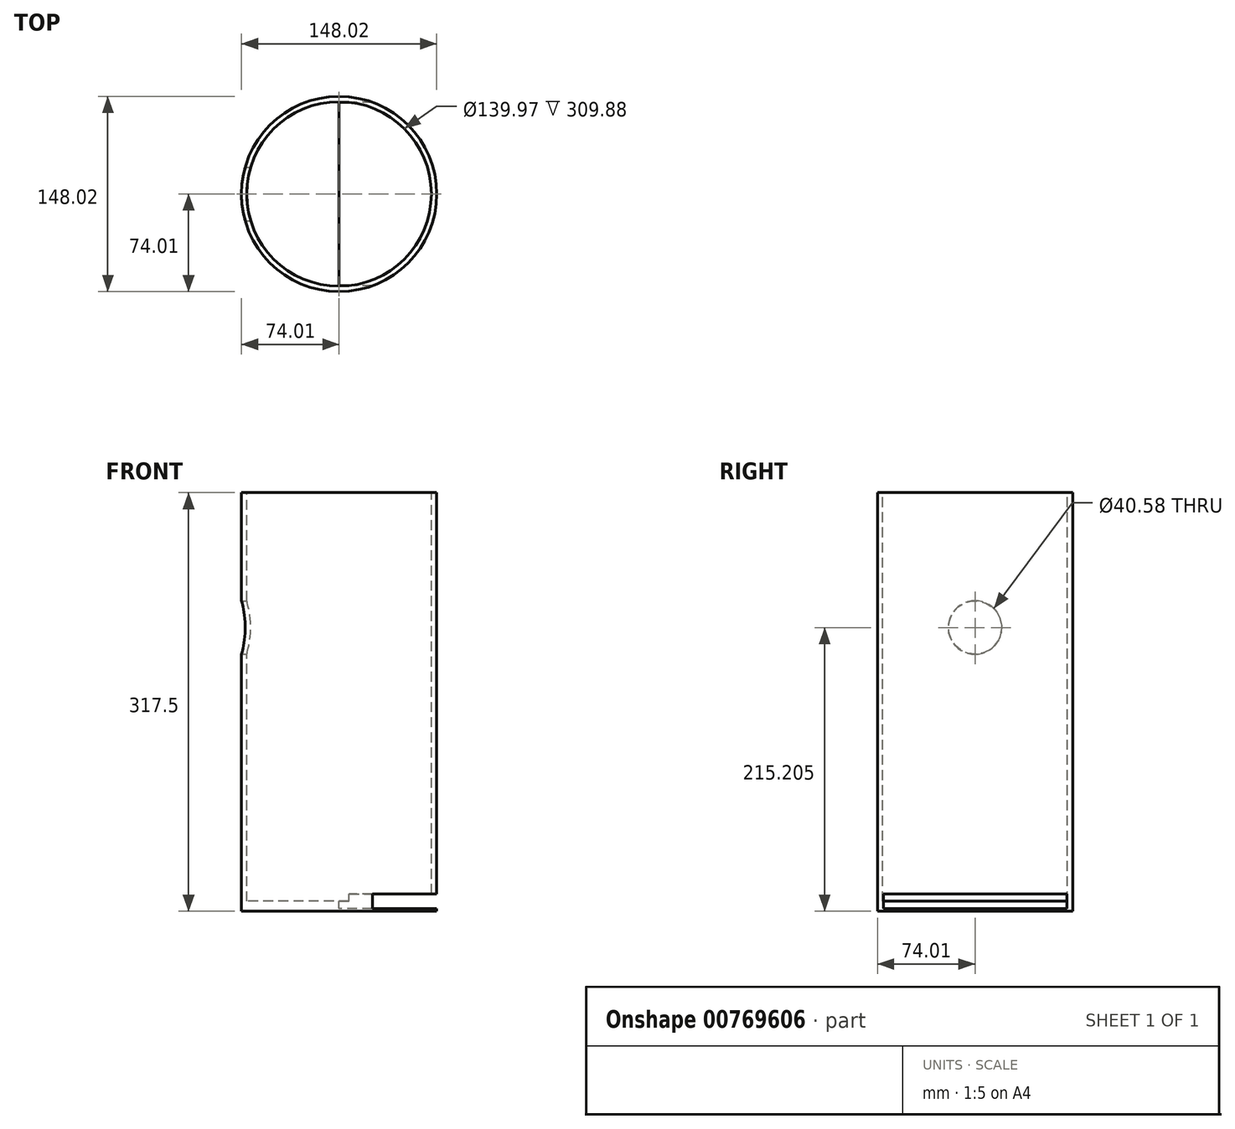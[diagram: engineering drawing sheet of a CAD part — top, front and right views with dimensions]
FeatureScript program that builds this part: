
annotation { "Feature Type Name" : "Feature", "Feature Type Description" : "" }
export const myFeature = defineFeature(function(context is Context, id is Id, definition is map)
    precondition{}
    {
        {
            var Q0;
            Q0=qCreatedBy(makeId("Top.planeOp"),FACE);
            var sketch = newSketch(context, id + "F0", { "sketchPlane" : qUnion([Q0])});
            skCircle(sketch, "E0", {"center": v(0, 0) * mm, "radius": 74 * mm});
            skSolve(sketch);
        }
        {
            var Q0;
            Q0=makeQuery(id+"F0.imprint","IMPRINT",FACE,{"disambiguationData":[TD([[makeQuery(id+"F0.imprint","IMPRINT",EDGE,{"derivedFrom":sQuery(id+"F0.wireOp",EDGE,"E0")}),1.0]])]});
            extrude(context, id + "F1", {"entities" : qUnion([Q0]), "depth" : 309.88 * mm, "offsetDistance" : 25.4 * mm});
        }
        {
            var Q0;
            Q0=makeQuery(id+"F1.opExtrude","CAP_FACE",FACE,{"disambiguationData":[OSD([sQuery(id+"F0.wireOp",EDGE,"E0")])],"isStart":false});
            var sketch = newSketch(context, id + "F2", { "sketchPlane" : qUnion([Q0])});
            skCircle(sketch, "E1", {"center": v(0, 0) * mm, "radius": 69.98 * mm});
            skSolve(sketch);
        }
        {
            var Q0;
            Q0=makeQuery(id+"F2.imprint","IMPRINT",FACE,{"disambiguationData":[TD([[makeQuery(id+"F2.imprint","IMPRINT",EDGE,{"derivedFrom":sQuery(id+"F2.wireOp",EDGE,"E1")}),1.0]])]});
            extrude(context, id + "F3", {"entities" : qUnion([Q0]), "operationType" : NewBodyOperationType.REMOVE, "oppositeDirection" : true, "depth" : 415.8 * mm, "offsetDistance" : 25.4 * mm});
        }
        {
            var Q0;
            Q0=qCreatedBy(makeId("Right.planeOp"),FACE);
            var sketch = newSketch(context, id + "F4", { "sketchPlane" : qUnion([Q0])});
            skCircle(sketch, "E2", {"center": v(0, 207.59) * mm, "radius": 20.3 * mm});
            skSolve(sketch);
        }
        {
            var Q0;
            Q0=makeQuery(id+"F4.imprint","IMPRINT",FACE,{"disambiguationData":[TD([[makeQuery(id+"F4.imprint","IMPRINT",EDGE,{"derivedFrom":sQuery(id+"F4.wireOp",EDGE,"E2")}),1.0]])]});
            extrude(context, id + "F5", {"entities" : qUnion([Q0]), "operationType" : NewBodyOperationType.REMOVE, "oppositeDirection" : true, "depth" : 138.94 * mm, "offsetDistance" : 25.4 * mm});
        }
        {
            var Q0;
            Q0 = qSketchRegion(id + "F0", true);
            extrude(context, id + "F6", {"entities" : qUnion([Q0]), "operationType" : NewBodyOperationType.ADD, "oppositeDirection" : true, "depth" : 7.62 * mm, "offsetDistance" : 25.4 * mm});
        }
        {
            var Q0;
            Q0=qCreatedBy(makeId("Right.planeOp"),FACE);
            var sketch = newSketch(context, id + "F7", { "sketchPlane" : qUnion([Q0])});
            skLineSegment(sketch, "E3.bottom", {"start": v(69.58, -5.55) * mm, "end": v(-69.58, -5.55) * mm});
            skLineSegment(sketch, "E3.top", {"start": v(69.58, 5.55) * mm, "end": v(-69.58, 5.55) * mm});
            skLineSegment(sketch, "E3.left", {"start": v(69.58, -5.55) * mm, "end": v(69.58, 5.55) * mm});
            skLineSegment(sketch, "E3.right", {"start": v(-69.58, -5.55) * mm, "end": v(-69.58, 5.55) * mm});
            skPoint(sketch, "E3.middle", {"position": v(0, 0) * mm});
            skSolve(sketch);
        }
        {
            var Q0;
            Q0=makeQuery(id+"F7.imprint","IMPRINT",FACE,{"disambiguationData":[TD([[makeQuery(id+"F7.imprint","IMPRINT",EDGE,{"derivedFrom":sQuery(id+"F7.wireOp",EDGE,"E3.bottom")}),-1.0]])]});
            extrude(context, id + "F8", {"entities" : qUnion([Q0]), "operationType" : NewBodyOperationType.REMOVE, "depth" : 97.28 * mm, "offsetDistance" : 25.4 * mm});
        }
    });
